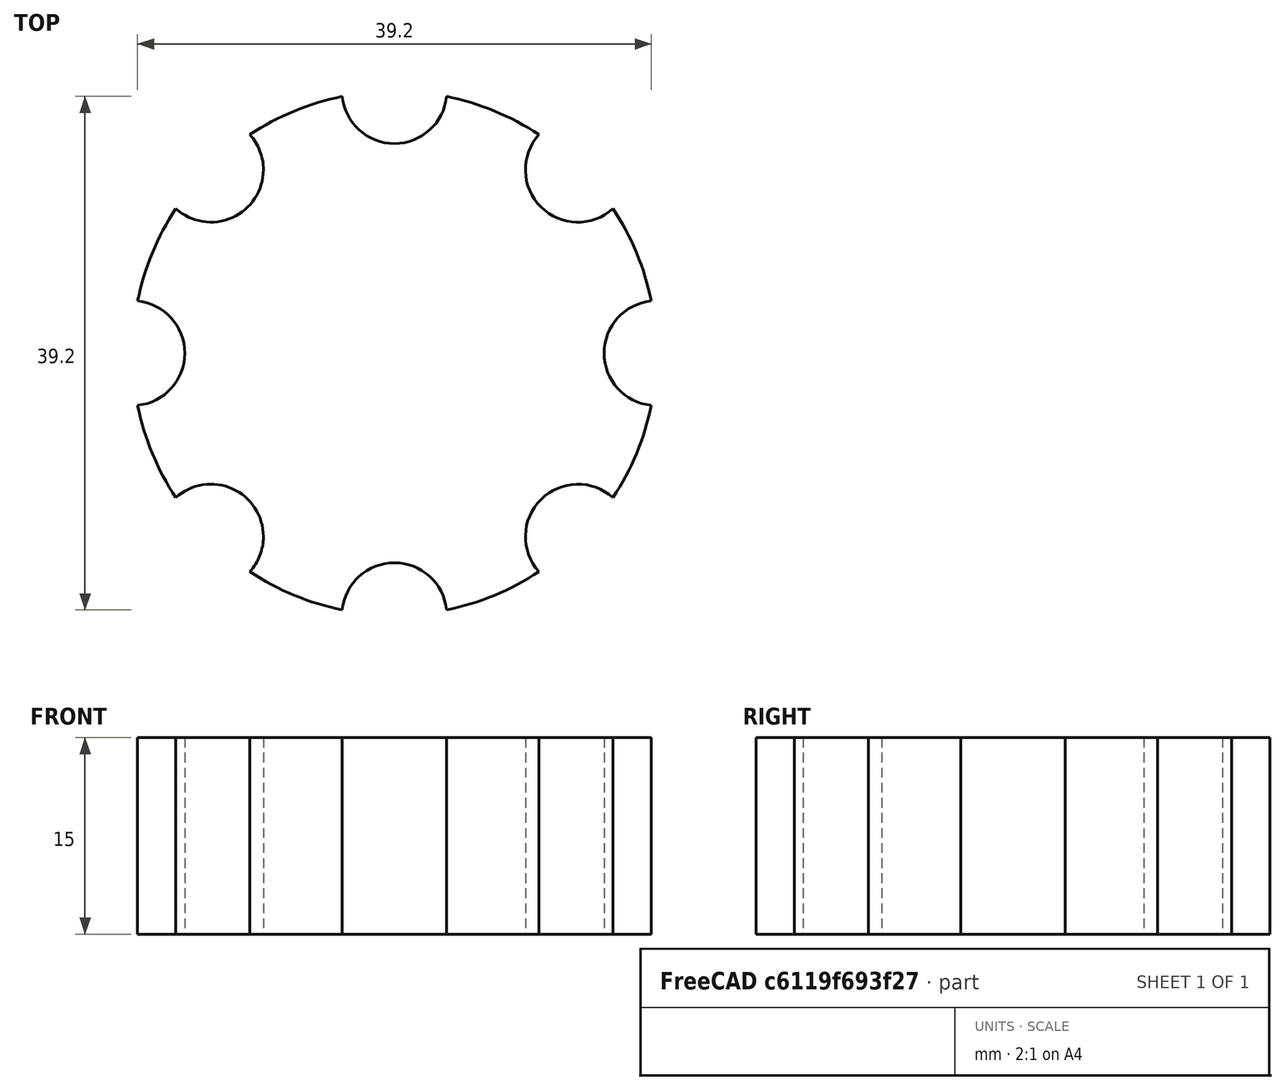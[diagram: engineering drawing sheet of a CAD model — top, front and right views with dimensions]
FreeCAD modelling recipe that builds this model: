
FCSTD DOCUMENT  (FreeCAD 0.21R33694 (Git))
Label: OJT1_T11R01_boton
License: All rights reserved
LicenseURL: http://en.wikipedia.org/wiki/All_rights_reserved
objects: Part::Cylinder×9, Part::Cut×8
note: 17 computed .brp shape members not serialized (recipe doc carries the construction recipe); baked Part::Feature solids carry a one-line shape summary decoded from their .brp

FEATURE [Part::Cylinder] Cylinder
  Angle = 360
  AttacherType = Attacher::AttachEngine3D
  FirstAngle = 0
  Height = 15
  Radius = 20
  SecondAngle = 0
FEATURE [Part::Cylinder] Cylinder001
  Angle = 360
  AttacherType = Attacher::AttachEngine3D
  FirstAngle = 0
  Height = 15
  Placement = pos=(20,0,0) rot=(0,0,1;0rad)
  Radius = 4
  SecondAngle = 0
FEATURE [Part::Cylinder] Cylinder002
  Angle = 360
  AttacherType = Attacher::AttachEngine3D
  FirstAngle = 0
  Height = 15
  Placement = pos=(0,20,0) rot=(0,0,1;0rad)
  Radius = 4
  SecondAngle = 0
FEATURE [Part::Cylinder] Cylinder003
  Angle = 360
  AttacherType = Attacher::AttachEngine3D
  FirstAngle = 0
  Height = 15
  Placement = pos=(-20,0,0) rot=(0,0,1;0rad)
  Radius = 4
  SecondAngle = 0
FEATURE [Part::Cylinder] Cylinder004
  Angle = 360
  AttacherType = Attacher::AttachEngine3D
  FirstAngle = 0
  Height = 15
  Placement = pos=(0,-20,0) rot=(0,0,1;0rad)
  Radius = 4
  SecondAngle = 0
FEATURE [Part::Cylinder] Cylinder005
  Angle = 360
  AttacherType = Attacher::AttachEngine3D
  FirstAngle = 0
  Height = 15
  Placement = pos=(14,-14,0) rot=(0,0,1;0rad)
  Radius = 4
  SecondAngle = 0
FEATURE [Part::Cylinder] Cylinder006
  Angle = 360
  AttacherType = Attacher::AttachEngine3D
  FirstAngle = 0
  Height = 15
  Placement = pos=(-14,14,0) rot=(0,0,1;0rad)
  Radius = 4
  SecondAngle = 0
FEATURE [Part::Cylinder] Cylinder007
  Angle = 360
  AttacherType = Attacher::AttachEngine3D
  FirstAngle = 0
  Height = 15
  Placement = pos=(-14,-14,0) rot=(0,0,1;0rad)
  Radius = 4
  SecondAngle = 0
FEATURE [Part::Cylinder] Cylinder008
  Angle = 360
  AttacherType = Attacher::AttachEngine3D
  FirstAngle = 0
  Height = 15
  Placement = pos=(14,14,0) rot=(0,0,1;0rad)
  Radius = 4
  SecondAngle = 0
FEATURE [Part::Cut] Cut
  Base = -> Cylinder
  Refine = true
  Tool = -> Cylinder001
FEATURE [Part::Cut] Cut001
  Base = -> Cut
  Refine = true
  Tool = -> Cylinder008
FEATURE [Part::Cut] Cut002
  Base = -> Cut001
  Refine = true
  Tool = -> Cylinder006
FEATURE [Part::Cut] Cut003
  Base = -> Cut002
  Refine = true
  Tool = -> Cylinder007
FEATURE [Part::Cut] Cut004
  Base = -> Cut003
  Refine = true
  Tool = -> Cylinder005
FEATURE [Part::Cut] Cut005
  Base = -> Cut004
  Refine = true
  Tool = -> Cylinder004
FEATURE [Part::Cut] Cut006
  Base = -> Cut005
  Refine = true
  Tool = -> Cylinder003
FEATURE [Part::Cut] Cut007
  Base = -> Cut006
  Refine = true
  Tool = -> Cylinder002
